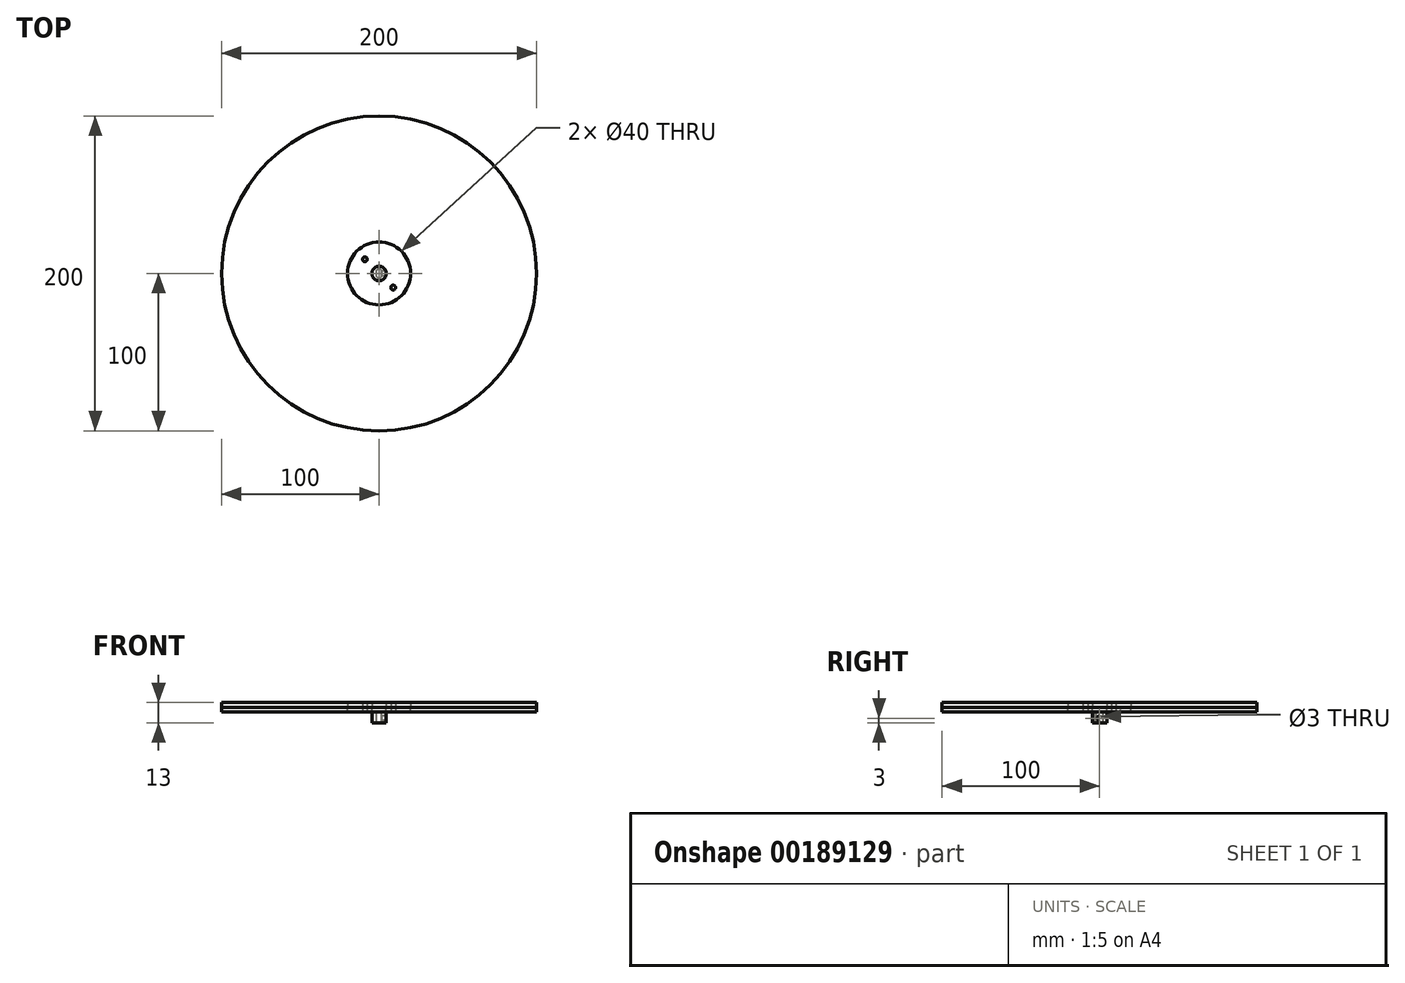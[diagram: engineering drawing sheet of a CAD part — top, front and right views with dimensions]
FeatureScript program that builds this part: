
annotation { "Feature Type Name" : "Feature", "Feature Type Description" : "" }
export const myFeature = defineFeature(function(context is Context, id is Id, definition is map)
    precondition{}
    {
        {
            var Q0;
            Q0=qCreatedBy(makeId("Top.planeOp"),FACE);
            var sketch = newSketch(context, id + "F0", { "sketchPlane" : qUnion([Q0])});
            skCircle(sketch, "E0", {"center": v(0, 0) * mm, "radius": 100 * mm});
            skSolve(sketch);
        }
        {
            var Q0;
            Q0=makeQuery(id+"F0.imprint","IMPRINT",FACE,{"disambiguationData":[TD([[makeQuery(id+"F0.imprint","IMPRINT",EDGE,{"derivedFrom":sQuery(id+"F0.wireOp",EDGE,"E0")}),1.0]])]});
            extrude(context, id + "F1", {"entities" : qUnion([Q0]), "depth" : 3 * mm});
        }
        {
            var Q0;
            Q0=makeQuery(id+"F1.opExtrude","CAP_FACE",FACE,{"disambiguationData":[OSD([sQuery(id+"F0.wireOp",EDGE,"E0")])],"isStart":true});
            var sketch = newSketch(context, id + "F2", { "sketchPlane" : qUnion([Q0])});
            skCircle(sketch, "E1", {"center": v(0, 0) * mm, "radius": 20 * mm});
            skSolve(sketch);
        }
        {
            var Q0;
            Q0=makeQuery(id+"F2.imprint","IMPRINT",FACE,{"disambiguationData":[TD([[makeQuery(id+"F2.imprint","IMPRINT",EDGE,{"derivedFrom":sQuery(id+"F2.wireOp",EDGE,"E1")}),1.0]])]});
            extrude(context, id + "F3", {"entities" : qUnion([Q0]), "depth" : 3 * mm});
        }
        {
            var Q0;
            Q0=makeQuery(id+"F3.opExtrude","CAP_FACE",FACE,{"disambiguationData":[OSD([sQuery(id+"F2.wireOp",EDGE,"E1")])],"isStart":false});
            var sketch = newSketch(context, id + "F4", { "sketchPlane" : qUnion([Q0])});
            skArc(sketch, "E2", {"start": v(-1.6, -2.05) * mm, "mid": v(0, -2.6) * mm, "end": v(1.6, -2.05) * mm});
            skCircle(sketch, "E3", {"center": v(0, 0) * mm, "radius": 4.6 * mm});
            skLineSegment(sketch, "E4", {"start": v(-1.6, 2.05) * mm, "end": v(-1.6, -2.05) * mm});
            skLineSegment(sketch, "E5.MirrorCS", {"start": v(1.6, 2.05) * mm, "end": v(1.6, -2.05) * mm});
            skArc(sketch, "E6.trimOffspring", {"start": v(1.6, 2.05) * mm, "mid": v(0, 2.6) * mm, "end": v(-1.6, 2.05) * mm});
            skSolve(sketch);
        }
        {
            var Q0;
            Q0=makeQuery(id+"F4.imprint","IMPRINT",FACE,{"disambiguationData":[TD([[makeQuery(id+"F4.imprint","IMPRINT",EDGE,{"derivedFrom":sQuery(id+"F4.wireOp",EDGE,"E2")}),-1.0]])]});
            extrude(context, id + "F5", {"entities" : qUnion([Q0]), "operationType" : NewBodyOperationType.ADD, "depth" : 7 * mm});
        }
        {
            var Q0;
            Q0=makeQuery(id+"F5.opExtrude","SWEPT_FACE",FACE,{"disambiguationData":[OSD([sQuery(id+"F4.wireOp",EDGE,"E5.MirrorCS")])]});
            var sketch = newSketch(context, id + "F6", { "sketchPlane" : qUnion([Q0])});
            skCircle(sketch, "E7", {"center": v(0, -7) * mm, "radius": 1.5 * mm});
            skSolve(sketch);
        }
        {
            var Q0;
            Q0=makeQuery(id+"F6.imprint","IMPRINT",FACE,{"disambiguationData":[TD([[makeQuery(id+"F6.imprint","IMPRINT",EDGE,{"derivedFrom":sQuery(id+"F6.wireOp",EDGE,"E7")}),1.0]])]});
            extrude(context, id + "F7", {"entities" : qUnion([Q0]), "operationType" : NewBodyOperationType.REMOVE, "oppositeDirection" : true, "depth" : 25 * mm});
        }
        {
            var Q0;
            Q0=makeQuery(id+"F1.opExtrude","CAP_FACE",FACE,{"disambiguationData":[OSD([sQuery(id+"F0.wireOp",EDGE,"E0")])],"isStart":true});
            var sketch = newSketch(context, id + "F8", { "sketchPlane" : qUnion([Q0])});
            skCircle(sketch, "E8.0", {"center": v(0, 0) * mm, "radius": 100 * mm});
            skCircle(sketch, "E9.0", {"center": v(0, 0) * mm, "radius": 20 * mm});
            skSolve(sketch);
        }
        {
            var Q0;
            Q0=makeQuery(id+"F8.imprint","IMPRINT",FACE,{"disambiguationData":[TD([[makeQuery(id+"F8.imprint","IMPRINT",EDGE,{"derivedFrom":sQuery(id+"F8.wireOp",EDGE,"E8.0")}),-1.0]])]});
            extrude(context, id + "F9", {"entities" : qUnion([Q0]), "depth" : 3 * mm});
        }
        {
            var Q0;
            {var subQ0=sQuery(id+"F2.wireOp",EDGE,"E1");Q0=makeQuery(id+"F5.boolean.opBoolean","SPLIT",FACE,{"disambiguationData":[TD([makeQuery(id+"F3.opExtrude","SWEPT_FACE",FACE,{"disambiguationData":[OSD([subQ0])]})])],"derivedFrom":makeQuery(id+"F3.opExtrude","CAP_FACE",FACE,{"disambiguationData":[OSD([subQ0])],"isStart":false})});}
            var sketch = newSketch(context, id + "F10", { "sketchPlane" : qUnion([Q0])});
            skCircle(sketch, "E10", {"center": v(-9, 9) * mm, "radius": 1.5 * mm});
            skCircle(sketch, "E11.MirrorC", {"center": v(9, 9) * mm, "radius": 1.5 * mm});
            skCircle(sketch, "E12.MirrorC", {"center": v(-9, -9) * mm, "radius": 1.5 * mm});
            skCircle(sketch, "E13.MirrorC", {"center": v(9, -9) * mm, "radius": 1.5 * mm});
            skSolve(sketch);
        }
        {
            var Q0;
            Q0=makeQuery(id+"F10.imprint","IMPRINT",FACE,{"disambiguationData":[TD([[makeQuery(id+"F10.imprint","IMPRINT",EDGE,{"derivedFrom":sQuery(id+"F10.wireOp",EDGE,"E10")}),1.0]])]});
            var Q1;
            Q1=makeQuery(id+"F10.imprint","IMPRINT",FACE,{"disambiguationData":[TD([[makeQuery(id+"F10.imprint","IMPRINT",EDGE,{"derivedFrom":sQuery(id+"F10.wireOp",EDGE,"E11.MirrorC")}),-1.0]])]});
            var Q2;
            Q2=makeQuery(id+"F10.imprint","IMPRINT",FACE,{"disambiguationData":[TD([[makeQuery(id+"F10.imprint","IMPRINT",EDGE,{"derivedFrom":sQuery(id+"F10.wireOp",EDGE,"E13.MirrorC")}),1.0]])]});
            var Q3;
            Q3=makeQuery(id+"F10.imprint","IMPRINT",FACE,{"disambiguationData":[TD([[makeQuery(id+"F10.imprint","IMPRINT",EDGE,{"derivedFrom":sQuery(id+"F10.wireOp",EDGE,"E12.MirrorC")}),-1.0]])]});
            extrude(context, id + "F11", {"entities" : qUnion([Q0, Q1, Q2, Q3]), "operationType" : NewBodyOperationType.REMOVE, "oppositeDirection" : true, "depth" : 25 * mm});
        }
    });
